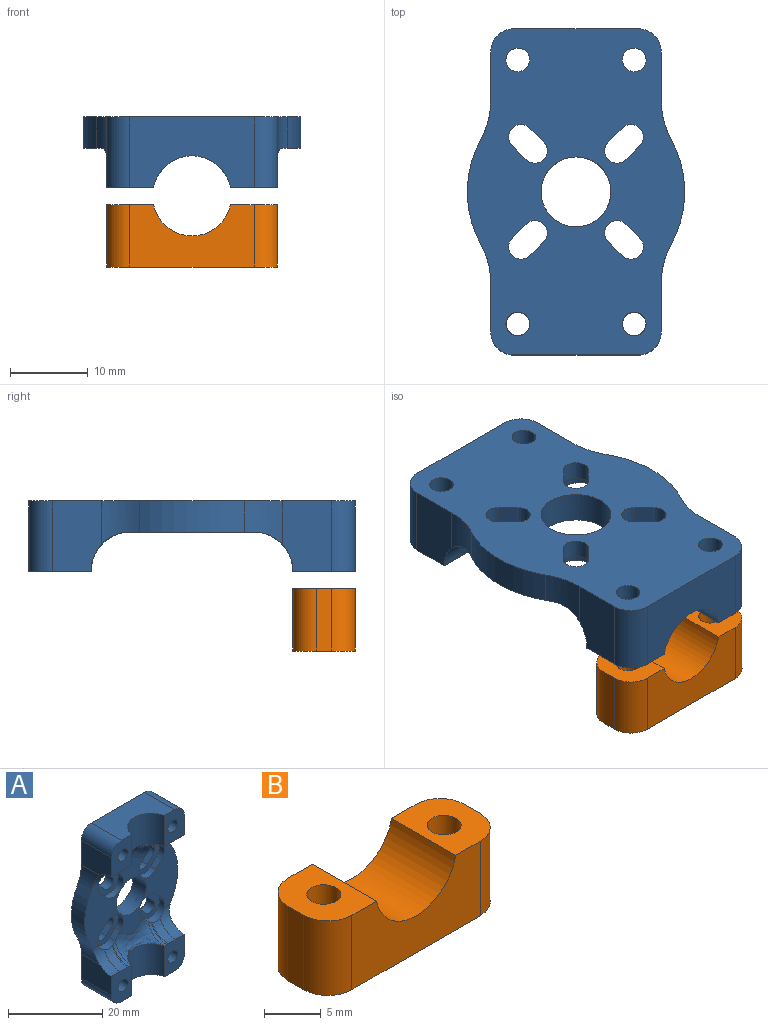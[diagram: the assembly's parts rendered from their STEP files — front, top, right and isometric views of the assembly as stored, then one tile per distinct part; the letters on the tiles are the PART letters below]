
ASSEMBLY  parts=2 mates=3
PART A: 87 faces, bbox 28.1x9.3x42.1 mm
  f0: plane 28x20mm, normal (0,-1,0), area 239.6mm2, adj f5,f9,f17,f22,f26,f31,f44,f50
  f1: plane 2.4x1.77mm, normal (0.71,0,-0.71), area 6mm2, adj f2,f4,f38,f82
  f2: cylinder r=1.6mm len=2.73mm, axis (0,-1,0), area 12.1mm2, adj f1,f3,f38,f82
  f3: plane 2.4x1.77mm, normal (-0.71,0,0.71), area 6mm2, adj f2,f4,f38,f82
  f4: cylinder r=1.6mm len=2.73mm, axis (0,-1,0), area 12.1mm2, adj f1,f3,f38,f82
  f5: bspline ~11.44x5.18mm, area 48.7mm2, adj f0,f6,f34,f48,f71,f84
  f6: cylinder r=5mm len=4.88mm, axis (1,0,0), area 5.1mm2, adj f5,f7,f42,f83,f84
  f7: bspline ~5.22x5.2mm, area 1.8mm2, adj f6,f8,f42,f83
  f8: bspline ~5.06x5.05mm, area 13.4mm2, adj f7,f9,f42,f83
  f9: cylinder r=5mm len=5mm, axis (1,0,0), area 20.7mm2, adj f0,f8,f42,f52,f65,f83
  f10: cylinder r=1.6mm len=2.73mm, axis (0,-1,0), area 12.1mm2, adj f11,f13,f38,f77
  f11: plane 2.4x1.77mm, normal (0.71,0,0.71), area 6mm2, adj f10,f12,f38,f77
  f12: cylinder r=1.6mm len=2.73mm, axis (0,-1,0), area 12.1mm2, adj f11,f13,f38,f77
  f13: plane 2.4x1.77mm, normal (-0.71,0,-0.71), area 6mm2, adj f10,f12,f38,f77
  f14: cylinder r=5mm len=4.88mm, axis (1,0,0), area 5.1mm2, adj f15,f26,f35,f78,f81
  f15: bspline ~5.9x5.86mm, area 1.8mm2, adj f14,f16,f35,f78
  f16: bspline ~5.21x5.19mm, area 13.4mm2, adj f15,f17,f35,f78
  f17: cylinder r=5mm len=5mm, axis (1,0,0), area 20.7mm2, adj f0,f16,f35,f54,f63,f78
  f18: plane 2.4x1.77mm, normal (-0.71,0,0.71), area 6mm2, adj f19,f21,f38,f72
  f19: cylinder r=1.6mm len=2.73mm, axis (0,-1,0), area 12.1mm2, adj f18,f20,f38,f72
  f20: plane 2.4x1.77mm, normal (0.71,0,-0.71), area 6mm2, adj f19,f21,f38,f72
  f21: cylinder r=1.6mm len=2.73mm, axis (0,-1,0), area 12.1mm2, adj f18,f20,f38,f72
  f22: cylinder r=5mm len=5mm, axis (1,0,0), area 20.7mm2, adj f0,f23,f40,f53,f64,f73
  f23: bspline ~5.3x5.29mm, area 13.4mm2, adj f22,f24,f40,f73
  f24: bspline ~5.91x5.87mm, area 1.8mm2, adj f23,f25,f40,f73
  f25: cylinder r=5mm len=4.88mm, axis (1,0,0), area 5.1mm2, adj f24,f26,f40,f73,f74
  f26: bspline ~11.44x5.18mm, area 48.7mm2, adj f0,f14,f25,f46,f74,f81
  f27: plane 2.4x1.77mm, normal (0.71,0,0.71), area 6mm2, adj f28,f30,f38,f67
  f28: cylinder r=1.6mm len=2.73mm, axis (0,-1,0), area 12.1mm2, adj f27,f29,f38,f67
  f29: plane 2.4x1.77mm, normal (-0.71,0,-0.71), area 6mm2, adj f28,f30,f38,f67
  f30: cylinder r=1.6mm len=2.73mm, axis (0,-1,0), area 12.1mm2, adj f27,f29,f38,f67
  f31: cylinder r=5mm len=5mm, axis (1,0,0), area 20.7mm2, adj f0,f32,f36,f49,f66,f68
  f32: bspline ~5.1x5.09mm, area 13.4mm2, adj f31,f33,f36,f68
  f33: bspline ~5.16x5.13mm, area 1.8mm2, adj f32,f34,f36,f68
  f34: cylinder r=5mm len=4.88mm, axis (1,0,0), area 5.1mm2, adj f5,f33,f36,f68,f71
  f35: plane 6.06x0.1mm, normal (0,0,-1), area 0.4mm2, adj f14,f15,f16,f17,f45,f46,f54
  f36: plane 6.06x0.1mm, normal (0,0,1), area 0.4mm2, adj f31,f32,f33,f34,f47,f48,f49
  f37: plane 16x9.05mm, normal (0,0,1), area 114.8mm2, adj f38,f39,f45,f46,f59,f60
  f38: plane 42x28mm, normal (0,1,0), area 833.1mm2, adj f1,f2,f3,f4,f10,f11,f12,f13
  f39: plane 8x6.05mm, normal (0,-1,0), area 39.2mm2, adj f37,f40,f46,f53,f57,f60
  f40: plane 6.06x0.1mm, normal (0,0,-1), area 0.4mm2, adj f22,f23,f24,f25,f39,f46,f53
  f41: plane 8x6.05mm, normal (0,-1,0), area 39.2mm2, adj f42,f43,f48,f52,f56,f61
  f42: plane 6.06x0.1mm, normal (0,0,1), area 0.4mm2, adj f6,f7,f8,f9,f41,f48,f52
  f43: plane 16x9.05mm, normal (0,0,-1), area 114.8mm2, adj f38,f41,f47,f48,f61,f62
  f44: cylinder r=4.5mm len=9mm, axis (0,1,0), area 113.1mm2, adj f0,f38
  f45: plane 8x6.05mm, normal (0,-1,0), area 39.2mm2, adj f35,f37,f46,f54,f58,f59
  f46: cylinder r=5.05mm len=9.9mm, axis (0,0,1), area 110.8mm2, adj f26,f35,f37,f39,f40,f45
  f47: plane 8x6.05mm, normal (0,-1,0), area 39.2mm2, adj f36,f43,f48,f49,f55,f62
  f48: cylinder r=5.05mm len=9.9mm, axis (0,0,-1), area 110.8mm2, adj f5,f36,f41,f42,f43,f47
  f49: plane 9.05x6.38mm, normal (1,0,0), area 54.4mm2, adj f31,f36,f38,f47,f62,f66
  f50: cylinder r=14mm len=13.56mm, axis (0,1,0), area 56.6mm2, adj f0,f38,f64,f66
  f51: cylinder r=14mm len=13.56mm, axis (0,1,0), area 56.6mm2, adj f0,f38,f63,f65
  f52: plane 9.05x6.38mm, normal (-1,0,0), area 54.4mm2, adj f9,f38,f41,f42,f61,f65
  f53: plane 9.05x6.38mm, normal (1,0,0), area 54.4mm2, adj f22,f38,f39,f40,f60,f64
  f54: plane 9.05x6.38mm, normal (-1,0,0), area 54.4mm2, adj f17,f35,f38,f45,f59,f63
  f55: cylinder r=1.53mm len=9.05mm, axis (0,1,0), area 86.7mm2, adj f38,f47
  f56: cylinder r=1.53mm len=9.05mm, axis (0,1,0), area 86.7mm2, adj f38,f41
  f57: cylinder r=1.53mm len=9.05mm, axis (0,1,0), area 86.7mm2, adj f38,f39
  f58: cylinder r=1.53mm len=9.05mm, axis (0,1,0), area 86.7mm2, adj f38,f45
  f59: cylinder r=3mm len=9.05mm, axis (0,1,0), area 42.6mm2, adj f37,f38,f45,f54
  f60: cylinder r=3mm len=9.05mm, axis (0,-1,0), area 42.6mm2, adj f37,f38,f39,f53
  f61: cylinder r=3mm len=9.05mm, axis (0,-1,0), area 42.6mm2, adj f38,f41,f43,f52
  f62: cylinder r=3mm len=9.05mm, axis (0,1,0), area 42.6mm2, adj f38,f43,f47,f49
  f63: cylinder r=10mm len=5.55mm, axis (0,1,0), area 23.1mm2, adj f0,f17,f38,f51,f54
  f64: cylinder r=10mm len=5.55mm, axis (0,1,0), area 23.1mm2, adj f0,f22,f38,f50,f53
  f65: cylinder r=10mm len=5.55mm, axis (0,1,0), area 23.1mm2, adj f0,f9,f38,f51,f52
  f66: cylinder r=10mm len=5.55mm, axis (0,1,0), area 23.1mm2, adj f0,f31,f38,f49,f50
  f67: plane 7.67x7.67mm, normal (0,-1,0), area 26mm2, adj f27,f28,f29,f30,f68,f69,f70,f71
  f68: cylinder r=2.95mm len=5.04mm, axis (0,1,0), area 16.3mm2, adj f0,f31,f32,f33,f34,f67,f69,f71
  f69: plane 1.77x1.77mm, normal (-0.71,0,-0.71), area 4mm2, adj f0,f67,f68,f70
  f70: cylinder r=2.95mm len=5.04mm, axis (0,1,0), area 14.8mm2, adj f0,f67,f69,f71
  f71: plane 1.9x1.9mm, normal (0.71,0,0.71), area 4.1mm2, adj f0,f5,f34,f67,f68,f70
  f72: plane 7.67x7.67mm, normal (0,-1,0), area 26mm2, adj f18,f19,f20,f21,f73,f74,f75,f76
  f73: cylinder r=2.95mm len=5.04mm, axis (0,1,0), area 16.3mm2, adj f0,f22,f23,f24,f25,f72,f74,f76
  f74: plane 1.9x1.9mm, normal (0.71,0,-0.71), area 4.1mm2, adj f0,f25,f26,f72,f73,f75
  f75: cylinder r=2.95mm len=5.04mm, axis (0,1,0), area 14.8mm2, adj f0,f72,f74,f76
  f76: plane 1.77x1.77mm, normal (-0.71,0,0.71), area 4mm2, adj f0,f72,f73,f75
  f77: plane 7.67x7.67mm, normal (0,-1,0), area 26mm2, adj f10,f11,f12,f13,f78,f79,f80,f81
  f78: cylinder r=2.95mm len=5.04mm, axis (0,1,0), area 16.3mm2, adj f0,f14,f15,f16,f17,f77,f79,f81
  f79: plane 1.77x1.77mm, normal (0.71,0,0.71), area 4mm2, adj f0,f77,f78,f80
  f80: cylinder r=2.95mm len=5.04mm, axis (0,1,0), area 14.8mm2, adj f0,f77,f79,f81
  f81: plane 1.9x1.9mm, normal (-0.71,0,-0.71), area 4.1mm2, adj f0,f14,f26,f77,f78,f80
  f82: plane 7.67x7.67mm, normal (0,-1,0), area 26mm2, adj f1,f2,f3,f4,f83,f84,f85,f86
  f83: cylinder r=2.95mm len=5.04mm, axis (0,1,0), area 16.3mm2, adj f0,f6,f7,f8,f9,f82,f84,f86
  f84: plane 1.9x1.9mm, normal (-0.71,0,0.71), area 4.1mm2, adj f0,f5,f6,f82,f83,f85
  f85: cylinder r=2.95mm len=5.04mm, axis (0,1,0), area 14.8mm2, adj f0,f82,f84,f86
  f86: plane 1.77x1.77mm, normal (0.71,0,-0.71), area 4mm2, adj f0,f82,f83,f85
PART B: 14 faces, bbox 22x8x8.1 mm
  f0: cylinder r=5.05mm len=9.9mm, axis (0,1,0), area 110.8mm2, adj f3,f4,f5,f9
  f1: plane 22x8mm, normal (0,0,-1), area 154.1mm2, adj f2,f4,f5,f6,f7,f8,f10,f11
  f2: plane 8.05x2mm, normal (1,0,0), area 16.1mm2, adj f1,f3,f7,f8
  f3: plane 8x6.05mm, normal (0,0,1), area 37.5mm2, adj f0,f2,f4,f5,f6,f7,f8
  f4: plane 16x8.05mm, normal (0,-1,0), area 98.8mm2, adj f0,f1,f3,f8,f9,f13
  f5: plane 16x8.05mm, normal (0,1,0), area 98.8mm2, adj f0,f1,f3,f7,f9,f12
  f6: cylinder r=1.5mm len=8.05mm, axis (0,0,1), area 75.9mm2, adj f1,f3
  f7: cylinder r=3mm len=8.05mm, axis (0,0,1), area 37.9mm2, adj f1,f2,f3,f5
  f8: cylinder r=3mm len=8.05mm, axis (0,0,-1), area 37.9mm2, adj f1,f2,f3,f4
  f9: plane 8x6.05mm, normal (0,0,1), area 37.5mm2, adj f0,f4,f5,f10,f11,f12,f13
  f10: plane 8.05x2mm, normal (-1,0,0), area 16.1mm2, adj f1,f9,f12,f13
  f11: cylinder r=1.5mm len=8.05mm, axis (0,0,1), area 75.9mm2, adj f1,f9
  f12: cylinder r=3mm len=8.05mm, axis (0,0,-1), area 37.9mm2, adj f1,f5,f9,f10
  f13: cylinder r=3mm len=8.05mm, axis (0,0,1), area 37.9mm2, adj f1,f4,f9,f10
PLACE A rot(axis=(1,0,0),90deg) t=(-14.45,-0.78,-3.77)mm
PLACE B rot(axis=(-0.9,0.08,-0.43),0deg) t=(-14.45,-13.78,-19.09)mm
MATE cylindrical A.f58 <-> B.f11  axis (0,0,1) through (-21.95,-17.78,0.23)mm
MATE planar A.f37 <-> B.f4  axis (0,-1,0) through (-22.45,-21.78,-4.3)mm
MATE parallel B.f9 <-> A.f45  axis (0,0,1) through (-19.4,-21.78,-11.04)mm
